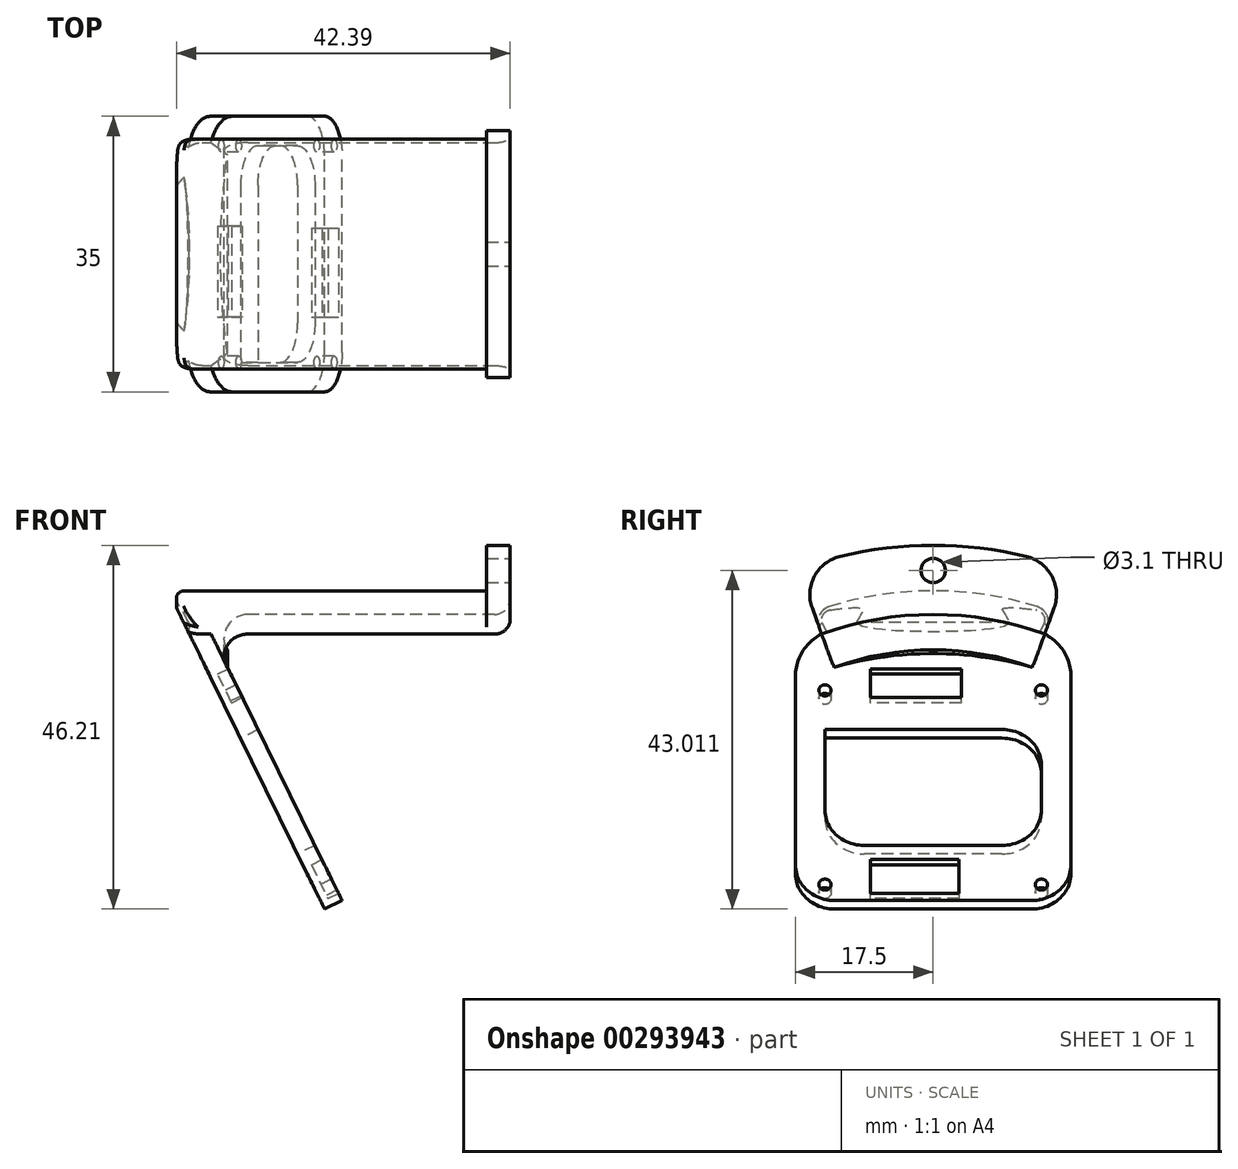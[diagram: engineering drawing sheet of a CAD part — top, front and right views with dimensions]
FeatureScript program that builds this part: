
annotation { "Feature Type Name" : "Feature", "Feature Type Description" : "" }
export const myFeature = defineFeature(function(context is Context, id is Id, definition is map)
    precondition{}
    {
        {
            var Q0;
            Q0=qCreatedBy(makeId("Front.planeOp"),FACE);
            var sketch = newSketch(context, id + "F0", { "sketchPlane" : qUnion([Q0])});
            skLineSegment(sketch, "E0", {"start": v(0, 0) * mm, "end": v(-27, 0) * mm});
            skLineSegment(sketch, "E1", {"start": v(-27, 0) * mm, "end": v(-38.4, 0) * mm});
            skLineSegment(sketch, "E2", {"start": v(-27, -22.73) * mm, "end": v(-27, 0) * mm, "construction": true});
            skLineSegment(sketch, "E3", {"start": v(-35.13, -8.66) * mm, "end": v(-39.26, -1.5) * mm});
            skLineSegment(sketch, "E4", {"start": v(-30.31, -3) * mm, "end": v(0, -3) * mm});
            skLineSegment(sketch, "E5", {"start": v(0, -3) * mm, "end": v(3, -3) * mm});
            skLineSegment(sketch, "E6", {"start": v(3, -3) * mm, "end": v(3, 5.78) * mm});
            skLineSegment(sketch, "E7", {"start": v(3, 5.78) * mm, "end": v(0, 5.78) * mm});
            skLineSegment(sketch, "E8", {"start": v(0, 5.78) * mm, "end": v(0, 0) * mm});
            skPoint(sketch, "E9.visualSharp", {"position": v(-35.5, -3) * mm});
            skArc(sketch, "E9.filletArc", {"start": v(-30.31, -3) * mm, "mid": v(-32.9, -4.5) * mm, "end": v(-32.9, -7.5) * mm});
            skLineSegment(sketch, "E10", {"start": v(-54.75, -44.42) * mm, "end": v(28.52, -44.42) * mm, "construction": true});
            skPoint(sketch, "E11.visualSharp", {"position": v(-40.13, 0) * mm});
            skArc(sketch, "E11.filletArc", {"start": v(-38.4, 0) * mm, "mid": v(-39.26, -0.5) * mm, "end": v(-39.26, -1.5) * mm});
            skLineSegment(sketch, "E12", {"start": v(-35.13, -8.66) * mm, "end": v(-32.9, -7.5) * mm});
            skSolve(sketch);
        }
        {
            var Q0;
            Q0=makeQuery(id+"F0.imprint","IMPRINT",FACE,{"disambiguationData":[TD([[makeQuery(id+"F0.imprint","IMPRINT",EDGE,{"derivedFrom":sQuery(id+"F0.wireOp",EDGE,"E0")}),1.0]])]});
            var Q1;
            Q1 = qConstructionFilter(qBodyType(qCreatedBy(id + "F0" ,EDGE), BodyType.WIRE), ConstructionObject.NO);
            var Q2;
            Q2=sQuery(id+"F0.wireOp",EDGE,"E10");
            revolve(context, id + "F1", {"surfaceOperationType" : NewSurfaceOperationType.NEW, "entities" : qUnion([Q0]), "surfaceEntities" : qUnion([Q1]), "axis" : qUnion([Q2]), "revolveType" : RevolveType.SYMMETRIC, "angle" : 40 * degree});
        }
        {
            var Q0;
            Q0=qCreatedBy(makeId("Front.planeOp"),FACE);
            var sketch = newSketch(context, id + "F2", { "sketchPlane" : qUnion([Q0])});
            skLineSegment(sketch, "E13.0", {"start": v(-35.13, -10.82) * mm, "end": v(-32.9, -9.73) * mm, "construction": true});
            skLineSegment(sketch, "E14", {"start": v(-35.13, -10.82) * mm, "end": v(-20.56, -40.43) * mm});
            skLineSegment(sketch, "E15", {"start": v(-20.56, -40.43) * mm, "end": v(-18.34, -39.34) * mm});
            skLineSegment(sketch, "E16", {"start": v(-18.34, -39.34) * mm, "end": v(-32.9, -9.73) * mm});
            skLineSegment(sketch, "E17", {"start": v(-32.9, -9.73) * mm, "end": v(-34.99, -5.5) * mm});
            skLineSegment(sketch, "E18", {"start": v(-34.99, -5.5) * mm, "end": v(-37.74, -5.5) * mm});
            skLineSegment(sketch, "E19", {"start": v(-37.74, -5.5) * mm, "end": v(-35.13, -10.82) * mm});
            skSolve(sketch);
        }
        {
            var Q0;
            Q0 = qSketchRegion(id + "F2", true);
            extrude(context, id + "F3", {"entities" : qUnion([Q0]), "operationType" : NewBodyOperationType.ADD, "depth" : 35 * mm, "offsetDistance" : 25 * mm, "symmetric" : true});
        }
        {
            var Q0;
            Q0=makeQuery(id+"F3.opExtrude","SWEPT_FACE",FACE,{"disambiguationData":[OSD([sQuery(id+"F2.wireOp",EDGE,"E14"),sQuery(id+"F2.wireOp",EDGE,"E19")])]});
            var sketch = newSketch(context, id + "F4", { "sketchPlane" : qUnion([Q0])});
            skLineSegment(sketch, "E20.bottom", {"start": v(13.75, -24.95) * mm, "end": v(-13.75, -24.95) * mm, "construction": true});
            skLineSegment(sketch, "E20.top", {"start": v(13.75, 2.55) * mm, "end": v(-13.75, 2.55) * mm, "construction": true});
            skLineSegment(sketch, "E20.left", {"start": v(13.75, -24.95) * mm, "end": v(13.75, 2.55) * mm, "construction": true});
            skLineSegment(sketch, "E20.right", {"start": v(-13.75, -24.95) * mm, "end": v(-13.75, 2.55) * mm, "construction": true});
            skCircle(sketch, "E21", {"center": v(-13.75, -24.95) * mm, "radius": 0.78 * mm});
            skCircle(sketch, "E22", {"center": v(13.75, -24.95) * mm, "radius": 0.78 * mm});
            skCircle(sketch, "E23", {"center": v(13.75, 2.55) * mm, "radius": 0.78 * mm});
            skCircle(sketch, "E24", {"center": v(-13.75, 2.55) * mm, "radius": 0.78 * mm});
            skLineSegment(sketch, "E25", {"start": v(0, -24.95) * mm, "end": v(0, -27.2) * mm, "construction": true});
            skLineSegment(sketch, "E26", {"start": v(-13.75, -11.2) * mm, "end": v(13.75, -11.2) * mm, "construction": true});
            skLineSegment(sketch, "E27.bottom", {"start": v(-13.75, -3) * mm, "end": v(13.75, -3) * mm});
            skLineSegment(sketch, "E27.top", {"start": v(-13.75, -19.4) * mm, "end": v(13.75, -19.4) * mm});
            skLineSegment(sketch, "E27.left", {"start": v(-13.75, -3) * mm, "end": v(-13.75, -19.4) * mm});
            skLineSegment(sketch, "E27.right", {"start": v(13.75, -3) * mm, "end": v(13.75, -19.4) * mm});
            skPoint(sketch, "E27.middle", {"position": v(0, -11.2) * mm});
            skSolve(sketch);
        }
        {
            var Q0;
            Q0 = qSketchRegion(id + "F4", true);
            var Q1;
            Q1 = qConstructionFilter(qBodyType(qCreatedBy(id + "F4" ,EDGE), BodyType.WIRE), ConstructionObject.NO);
            extrude(context, id + "F5", {"entities" : qUnion([Q0]), "operationType" : NewBodyOperationType.REMOVE, "surfaceEntities" : qUnion([Q1]), "oppositeDirection" : true, "depth" : 5.2 * mm, "offsetDistance" : 25 * mm});
        }
        {
            var Q0;
            Q0=makeQuery(id+"F5.boolean.opBoolean","COPY",EDGE,{"derivedFrom":makeQuery(id+"F5.opExtrude","SWEPT_EDGE",EDGE,{"disambiguationData":[OSD([sQuery(id+"F4.wireOp",EDGE,"E27.bottom"),sQuery(id+"F4.wireOp",EDGE,"E27.left")])]})});
            var Q1;
            Q1=makeQuery(id+"F5.boolean.opBoolean","COPY",EDGE,{"derivedFrom":makeQuery(id+"F5.opExtrude","SWEPT_EDGE",EDGE,{"disambiguationData":[OSD([sQuery(id+"F4.wireOp",EDGE,"E27.top"),sQuery(id+"F4.wireOp",EDGE,"E27.right")])]})});
            var Q2;
            Q2=makeQuery(id+"F5.boolean.opBoolean","COPY",EDGE,{"derivedFrom":makeQuery(id+"F5.opExtrude","SWEPT_EDGE",EDGE,{"disambiguationData":[OSD([sQuery(id+"F4.wireOp",EDGE,"E27.top"),sQuery(id+"F4.wireOp",EDGE,"E27.left")])]})});
            fillet(context, id + "F6", {"entities" : qUnion([Q0, Q1, Q2]), "tangentPropagation" : true, "radius" : 5 * mm, "defaultsChanged" : false, "vertexSettings" : [], "allowEdgeOverflow" : false});
        }
        {
            var Q0;
            Q0=makeQuery(id+"F3.boolean.opBoolean","INTERSECT",EDGE,{"derivedFrom":[makeQuery(id+"F1.opRevolve","SWEPT_FACE",FACE,{"disambiguationData":[OSD([sQuery(id+"F0.wireOp",EDGE,"E3")])]}),makeQuery(id+"F3.opExtrude","SWEPT_FACE",FACE,{"disambiguationData":[OSD([sQuery(id+"F2.wireOp",EDGE,"E18")])]})]});
            fillet(context, id + "F7", {"entities" : qUnion([Q0]), "tangentPropagation" : true, "radius" : 1 * mm, "defaultsChanged" : true, "vertexSettings" : [], "allowEdgeOverflow" : false});
        }
        {
            var Q0;
            Q0=makeQuery(id+"F3.opExtrude","CAP_EDGE",EDGE,{"disambiguationData":[OSD([sQuery(id+"F2.wireOp",EDGE,"E18")])],"isStart":true});
            var Q1;
            Q1=makeQuery(id+"F3.opExtrude","CAP_EDGE",EDGE,{"disambiguationData":[OSD([sQuery(id+"F2.wireOp",EDGE,"E18")])],"isStart":false});
            fillet(context, id + "F8", {"entities" : qUnion([Q0, Q1]), "tangentPropagation" : true, "radius" : 6 * mm, "defaultsChanged" : true, "vertexSettings" : [], "allowEdgeOverflow" : false});
        }
        {
            var Q0;
            Q0=makeQuery(id+"F1.opRevolve","CAP_EDGE",EDGE,{"disambiguationData":[OSD([sQuery(id+"F0.wireOp",EDGE,"E3")])],"isStart":false});
            var Q1;
            Q1=makeQuery(id+"F1.opRevolve","CAP_EDGE",EDGE,{"disambiguationData":[OSD([sQuery(id+"F0.wireOp",EDGE,"E3")])],"isStart":true});
            fillet(context, id + "F9", {"entities" : qUnion([Q0, Q1]), "tangentPropagation" : true, "radius" : 2 * mm, "defaultsChanged" : false, "vertexSettings" : [], "allowEdgeOverflow" : false});
        }
        {
            var Q0;
            Q0=makeQuery(id+"F1.opRevolve","SWEPT_EDGE",EDGE,{"disambiguationData":[OSD([sQuery(id+"F0.wireOp",EDGE,"E5"),sQuery(id+"F0.wireOp",EDGE,"E6")])]});
            fillet(context, id + "F10", {"entities" : qUnion([Q0]), "tangentPropagation" : true, "radius" : 2 * mm, "defaultsChanged" : true, "vertexSettings" : [], "allowEdgeOverflow" : false});
        }
        {
            var Q0;
            Q0=makeQuery(id+"F3.opExtrude","SWEPT_FACE",FACE,{"disambiguationData":[OSD([sQuery(id+"F2.wireOp",EDGE,"E14"),sQuery(id+"F2.wireOp",EDGE,"E19")])]});
            var sketch = newSketch(context, id + "F11", { "sketchPlane" : qUnion([Q0])});
            skLineSegment(sketch, "E28.bottom", {"start": v(-44, 27.69) * mm, "end": v(48.71, 27.69) * mm});
            skLineSegment(sketch, "E28.top", {"start": v(-44, -34.34) * mm, "end": v(48.71, -34.34) * mm});
            skLineSegment(sketch, "E28.left", {"start": v(-44, 27.69) * mm, "end": v(-44, -34.34) * mm});
            skLineSegment(sketch, "E28.right", {"start": v(48.71, 27.69) * mm, "end": v(48.71, -34.34) * mm});
            skSolve(sketch);
        }
        {
            var Q0;
            Q0 = qSketchRegion(id + "F11", true);
            extrude(context, id + "F12", {"entities" : qUnion([Q0]), "operationType" : NewBodyOperationType.REMOVE, "depth" : 25 * mm, "offsetDistance" : 25 * mm});
        }
        {
            var Q0;
            Q0=makeQuery(id+"F3.opExtrude","CAP_EDGE",EDGE,{"disambiguationData":[OSD([sQuery(id+"F2.wireOp",EDGE,"E15")])],"isStart":true});
            var Q1;
            Q1=makeQuery(id+"F3.opExtrude","CAP_EDGE",EDGE,{"disambiguationData":[OSD([sQuery(id+"F2.wireOp",EDGE,"E15")])],"isStart":false});
            fillet(context, id + "F13", {"entities" : qUnion([Q0, Q1]), "tangentPropagation" : true, "radius" : 5 * mm, "defaultsChanged" : false, "vertexSettings" : [], "allowEdgeOverflow" : false});
        }
        {
            var Q0;
            Q0=makeQuery(id+"F1.opRevolve","SWEPT_FACE",FACE,{"disambiguationData":[OSD([sQuery(id+"F0.wireOp",EDGE,"E6")])]});
            var sketch = newSketch(context, id + "F14", { "sketchPlane" : qUnion([Q0])});
            skCircle(sketch, "E29", {"center": v(0, 2.58) * mm, "radius": 1.55 * mm});
            skPoint(sketch, "E30.0", {"position": v(0, -22.73) * mm});
            skPoint(sketch, "E30.1", {"position": v(0, -44.42) * mm});
            skSolve(sketch);
        }
        {
            var Q0;
            Q0 = qSketchRegion(id + "F14", true);
            extrude(context, id + "F15", {"entities" : qUnion([Q0]), "operationType" : NewBodyOperationType.REMOVE, "oppositeDirection" : true, "depth" : 25 * mm, "offsetDistance" : 25 * mm});
        }
        {
            var Q0;
            Q0=makeQuery(id+"F1.opRevolve","CAP_EDGE",EDGE,{"disambiguationData":[OSD([sQuery(id+"F0.wireOp",EDGE,"E7")])],"isStart":false});
            var Q1;
            Q1=makeQuery(id+"F1.opRevolve","CAP_EDGE",EDGE,{"disambiguationData":[OSD([sQuery(id+"F0.wireOp",EDGE,"E7")])],"isStart":true});
            fillet(context, id + "F16", {"entities" : qUnion([Q0, Q1]), "tangentPropagation" : true, "radius" : 5 * mm, "defaultsChanged" : false, "vertexSettings" : [], "allowEdgeOverflow" : false});
        }
        {
            var Q0;
            Q0=makeQuery(id+"F3.opExtrude","SWEPT_FACE",FACE,{"disambiguationData":[OSD([sQuery(id+"F2.wireOp",EDGE,"E16"),sQuery(id+"F2.wireOp",EDGE,"E17")])]});
            var sketch = newSketch(context, id + "F17", { "sketchPlane" : qUnion([Q0])});
            skLineSegment(sketch, "E31.bottom", {"start": v(3.28, -21.4) * mm, "end": v(-7.98, -21.4) * mm});
            skLineSegment(sketch, "E31.top", {"start": v(3.28, -26.2) * mm, "end": v(-7.98, -26.2) * mm});
            skLineSegment(sketch, "E31.left", {"start": v(3.28, -21.4) * mm, "end": v(3.28, -26.2) * mm});
            skLineSegment(sketch, "E31.right", {"start": v(-7.98, -21.4) * mm, "end": v(-7.98, -26.2) * mm});
            skLineSegment(sketch, "E32.bottom", {"start": v(3.58, 1.53) * mm, "end": v(-7.98, 1.53) * mm});
            skLineSegment(sketch, "E32.top", {"start": v(3.58, 5.6) * mm, "end": v(-7.98, 5.6) * mm});
            skLineSegment(sketch, "E32.left", {"start": v(3.58, 1.53) * mm, "end": v(3.58, 5.6) * mm});
            skLineSegment(sketch, "E32.right", {"start": v(-7.98, 1.53) * mm, "end": v(-7.98, 5.6) * mm});
            skSolve(sketch);
        }
        {
            var Q0;
            Q0 = qSketchRegion(id + "F17", true);
            extrude(context, id + "F18", {"entities" : qUnion([Q0]), "operationType" : NewBodyOperationType.REMOVE, "oppositeDirection" : true, "depth" : 1.5 * mm, "offsetDistance" : 25 * mm});
        }
    });
